FCSTD DOCUMENT  (FreeCAD 0.21R33668 +26 (Git))
Label: doigt_index_prothese
License: All rights reserved
LicenseURL: http://en.wikipedia.org/wiki/All_rights_reserved
objects: Part::Feature×7, PartDesign::CoordinateSystem×6, PartDesign::FeatureBase×6, PartDesign::Body×6, Part::FeaturePython×1, App::AnnotationLabel×1, App::DocumentObjectGroup×1
note: 26 computed .brp shape members not serialized (recipe doc carries the construction recipe); baked Part::Feature solids carry a one-line shape summary decoded from their .brp

FEATURE [PartDesign::CoordinateSystem] LCS_0
  AttacherType = Attacher::AttachEngine3D
  MapMode = 2
  Support = -> [X_Axis]
FEATURE [Part::Feature] finger_base_knuckle_v3_5_006_solid  label="finger_base_knuckle_v3_5_006 (Solid)"
  shape: bbox 18.5 x 17.25 x 15.15 mm, 17542 faces (baked)
FEATURE [PartDesign::FeatureBase] BaseFeature
  BaseFeature = -> finger_base_knuckle_v3_5_006_solid
FEATURE [PartDesign::Body] Body  label="finger_base_knuckle"
  BaseFeature = -> finger_base_knuckle_v3_5_006_solid
  Group = -> [BaseFeature,LCS_0]
  Origin = -> Origin
  Placement = pos=(0,0,6) rot=(0,0,1;0rad)
  Tip = -> BaseFeature
FEATURE [PartDesign::CoordinateSystem] LCS_001
  AttacherType = Attacher::AttachEngine3D
  MapMode = 2
  Support = -> [X_Axis001]
FEATURE [Part::Feature] dangercreations_finger_v3_5_5_index_middle_bumper001_solid  label="dangercreations_finger_v3_5_5_index_middle_bumper001 (Solid)"
  shape: bbox 11.89 x 15.5 x 6 mm, 3652 faces (baked)
FEATURE [PartDesign::FeatureBase] BaseFeature001
  BaseFeature = -> dangercreations_finger_v3_5_5_index_middle_bumper001_solid
FEATURE [PartDesign::Body] middle_bumper
  BaseFeature = -> dangercreations_finger_v3_5_5_index_middle_bumper001_solid
  Group = -> [BaseFeature001,LCS_001]
  Origin = -> Origin001
  Placement = pos=(0,0,20) rot=(0,0,1;0rad)
  Tip = -> BaseFeature001
FEATURE [PartDesign::CoordinateSystem] LCS_002
  AttacherType = Attacher::AttachEngine3D
  MapMode = 2
  Support = -> [X_Axis002]
FEATURE [Part::Feature] dangercreations_finger_v3_5_5_index_middle_segment001_solid  label="dangercreations_finger_v3_5_5_index_middle_segment001 (Solid)"
  shape: bbox 28 x 12.5 x 8.52 mm, 17486 faces (baked)
FEATURE [PartDesign::FeatureBase] BaseFeature002
  BaseFeature = -> dangercreations_finger_v3_5_5_index_middle_segment001_solid
FEATURE [PartDesign::Body] middle_segment
  BaseFeature = -> dangercreations_finger_v3_5_5_index_middle_segment001_solid
  Group = -> [BaseFeature002,LCS_002]
  Origin = -> Origin002
  Placement = pos=(-3e-15,0,34) rot=(0,1,0;1.5708rad)
  Tip = -> BaseFeature002
FEATURE [Part::Feature] dangercreations_finger_v3_5_5_index_finger_socket001_solid  label="dangercreations_finger_v3_5_5_index_finger_socket001 (Solid)"
  shape: bbox 23.06 x 23.04 x 71 mm, 6810 faces (baked)
FEATURE [PartDesign::CoordinateSystem] LCS_003
  AttacherType = Attacher::AttachEngine3D
  MapMode = 2
  Support = -> [X_Axis003]
FEATURE [Part::Feature] dangercreations_finger_v3_5_5_index_finger_socket001_solid001  label="dangercreations_finger_v3_5_5_index_finger_socket001 (Solid)001"
  shape: bbox 23.06 x 23.04 x 71 mm, 6810 faces (baked)
FEATURE [PartDesign::FeatureBase] BaseFeature003
  BaseFeature = -> dangercreations_finger_v3_5_5_index_finger_socket001_solid001
FEATURE [PartDesign::Body] index_socket
  BaseFeature = -> dangercreations_finger_v3_5_5_index_finger_socket001_solid001
  Group = -> [BaseFeature003,LCS_003]
  Origin = -> Origin003
  Placement = pos=(0,9e-15,-14) rot=(0,1,0;3.14159rad)
  Tip = -> BaseFeature003
FEATURE [PartDesign::CoordinateSystem] LCS_004
  AttacherType = Attacher::AttachEngine3D
  MapMode = 2
  Support = -> [X_Axis004]
FEATURE [Part::Feature] dangercreations_finger_v3_5_5_index_tip_cover001_solid  label="dangercreations_finger_v3_5_5_index_tip_cover001 (Solid)"
  Placement = pos=(0,0,102) rot=(0,0,1;0rad)
  shape: bbox 13.5 x 13.08 x 20.4 mm, 6572 faces (baked)
FEATURE [PartDesign::FeatureBase] BaseFeature004
  BaseFeature = -> dangercreations_finger_v3_5_5_index_tip_cover001_solid
FEATURE [PartDesign::Body] tip_cover
  BaseFeature = -> dangercreations_finger_v3_5_5_index_tip_cover001_solid
  Group = -> [BaseFeature004,LCS_004]
  Origin = -> Origin004
  Placement = pos=(0,0,84) rot=(0,0,1;0rad)
  Tip = -> BaseFeature004
FEATURE [PartDesign::CoordinateSystem] LCS_005
  AttacherType = Attacher::AttachEngine3D
  MapMode = 2
  Support = -> [X_Axis005]
FEATURE [Part::Feature] dangercreations_finger_v3_5_5_index_tip_knuckle001_solid  label="dangercreations_finger_v3_5_5_index_tip_knuckle001 (Solid)"
  shape: bbox 15.5 x 18.5 x 13 mm, 13648 faces (baked)
FEATURE [PartDesign::FeatureBase] BaseFeature005
  BaseFeature = -> dangercreations_finger_v3_5_5_index_tip_knuckle001_solid
FEATURE [PartDesign::Body] Body_2  label="tip_knuckle"
  BaseFeature = -> dangercreations_finger_v3_5_5_index_tip_knuckle001_solid
  Group = -> [BaseFeature005,LCS_005]
  Origin = -> Origin005
  Placement = pos=(0,-1e-14,47) rot=(1,0,0;1.5708rad)
  Tip = -> BaseFeature005
FEATURE [Part::FeaturePython] DistPoints  # WARN: FeaturePython — macro-defined, semantics opaque (R4)
FEATURE [App::AnnotationLabel] MeasureLbl
  BasePosition = (-4.25,-0.0706348,41.9223)
  LabelText = D = 18,00 mm
  TextPosition = (0,0,0)
FEATURE [App::DocumentObjectGroup] Measures
  Group = -> [DistPoints,MeasureLbl]
